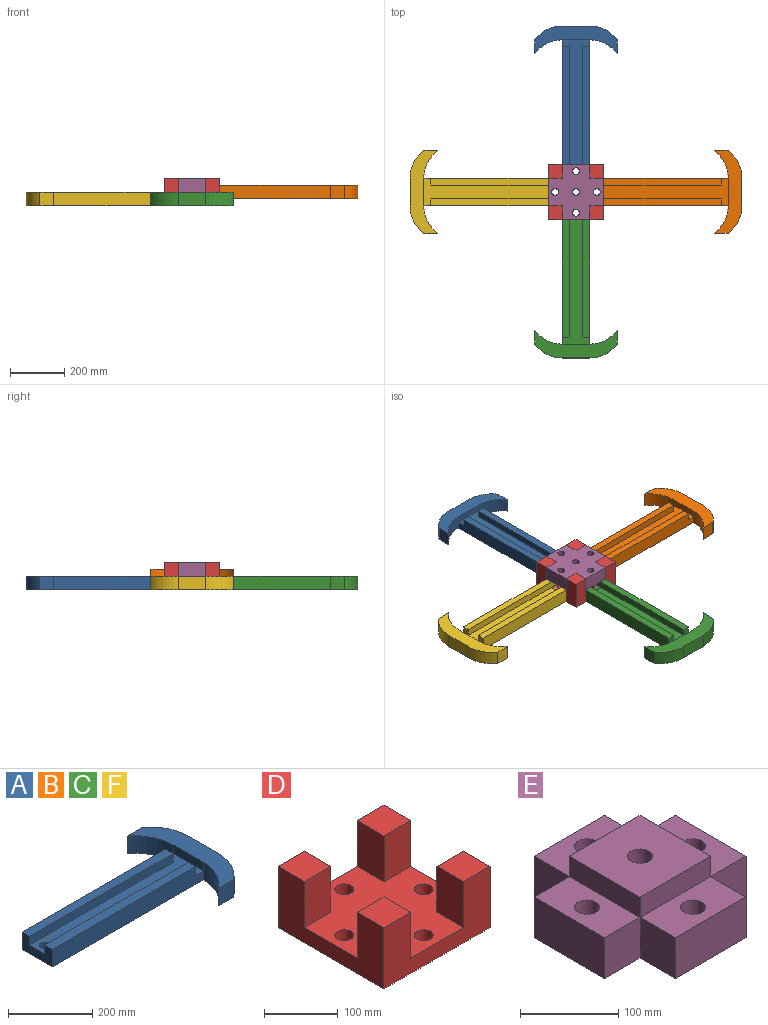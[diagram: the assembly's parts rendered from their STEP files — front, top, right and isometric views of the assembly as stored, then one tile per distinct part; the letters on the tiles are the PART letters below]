
ASSEMBLY  parts=6 mates=5
PART A: 21 faces, bbox 558.8x304.8x50.8 mm
  f0: plane 508x50.8mm, normal (0,-1,0), area 25161.2mm2, adj f4,f5,f12,f14,f19,f20
  f1: plane 508x50.8mm, normal (0,1,0), area 25161.2mm2, adj f11,f12,f13,f14,f16,f20
  f2: cylinder r=12.7mm len=25.4mm, axis (0,0,-1), area 2026.8mm2, adj f14,f20
  f3: plane 304.8x101.6mm, normal (0,0,1), area 15483.8mm2, adj f5,f6,f7,f8,f9,f10,f11,f15
  f4: plane 482.6x25.4mm, normal (0,0,1), area 12258mm2, adj f0,f12,f18,f19
  f5: cylinder r=127mm len=101.6mm, axis (0,0,-1), area 5982.5mm2, adj f0,f3,f6,f14,f15
  f6: plane 50.8x50.8mm, normal (0,-1,0), area 2580.6mm2, adj f3,f5,f7,f14
  f7: cylinder r=127mm len=101.6mm, axis (0,0,-1), area 5982.5mm2, adj f3,f6,f8,f14
  f8: plane 101.6x50.8mm, normal (1,0,0), area 5161.3mm2, adj f3,f7,f9,f14
  f9: cylinder r=127mm len=101.6mm, axis (0,0,-1), area 5982.5mm2, adj f3,f8,f10,f14
  f10: plane 50.8x50.8mm, normal (0,1,0), area 2580.6mm2, adj f3,f9,f11,f14
  f11: cylinder r=127mm len=101.6mm, axis (0,0,-1), area 5982.5mm2, adj f1,f3,f10,f14,f15
  f12: plane 101.6x50.8mm, normal (-1,0,0), area 3871mm2, adj f0,f1,f4,f13,f14,f17,f18,f20
  f13: plane 482.6x25.4mm, normal (0,0,1), area 12258mm2, adj f1,f12,f16,f17
  f14: plane 558.8x304.8mm, normal (0,0,-1), area 66589.9mm2, adj f0,f1,f2,f5,f6,f7,f8,f9
  f15: plane 101.6x25.4mm, normal (-1,0,0), area 2580.6mm2, adj f3,f5,f11,f20
  f16: plane 25.4x25.4mm, normal (1,0,0), area 645.2mm2, adj f1,f13,f17,f20
  f17: plane 482.6x25.4mm, normal (0,-1,0), area 12258mm2, adj f12,f13,f16,f20
  f18: plane 482.6x25.4mm, normal (0,1,0), area 12258mm2, adj f4,f12,f19,f20
  f19: plane 25.4x25.4mm, normal (1,0,0), area 645.2mm2, adj f0,f4,f18,f20
  f20: plane 508x101.6mm, normal (0,0,1), area 26590mm2, adj f0,f1,f2,f12,f15,f16,f17,f18
PART B: same geometry as A
PART C: same geometry as A
PART D: 23 faces, bbox 203.2x203.2x101.6 mm
  f0: plane 203.2x101.6mm, normal (1,0,0), area 12903.2mm2, adj f5,f8,f9,f10,f13,f20,f21,f22
  f1: cylinder r=12.7mm len=25.4mm, axis (0,0,-1), area 2026.8mm2, adj f13,f22
  f2: cylinder r=12.7mm len=25.4mm, axis (0,0,-1), area 2026.8mm2, adj f13,f22
  f3: cylinder r=12.7mm len=25.4mm, axis (0,0,-1), area 2026.8mm2, adj f13,f22
  f4: cylinder r=12.7mm len=25.4mm, axis (0,0,-1), area 2026.8mm2, adj f13,f22
  f5: plane 203.2x101.6mm, normal (0,-1,0), area 12903.2mm2, adj f0,f7,f8,f11,f13,f18,f19,f22
  f6: cylinder r=12.7mm len=25.4mm, axis (0,0,-1), area 2026.8mm2, adj f13,f22
  f7: plane 50.8x50.8mm, normal (0,0,1), area 2580.6mm2, adj f5,f11,f17,f18
  f8: plane 50.8x50.8mm, normal (0,0,1), area 2580.6mm2, adj f0,f5,f19,f20
  f9: plane 50.8x50.8mm, normal (0,0,1), area 2580.6mm2, adj f0,f10,f14,f21
  f10: plane 203.2x101.6mm, normal (0,1,0), area 12903.2mm2, adj f0,f9,f11,f12,f13,f14,f15,f22
  f11: plane 203.2x101.6mm, normal (-1,0,0), area 12903.2mm2, adj f5,f7,f10,f12,f13,f16,f17,f22
  f12: plane 50.8x50.8mm, normal (0,0,1), area 2580.6mm2, adj f10,f11,f15,f16
  f13: plane 203.2x203.2mm, normal (0,0,-1), area 38756.7mm2, adj f0,f1,f2,f3,f4,f5,f6,f10
  f14: plane 76.2x50.8mm, normal (-1,0,0), area 3871mm2, adj f9,f10,f21,f22
  f15: plane 76.2x50.8mm, normal (1,0,0), area 3871mm2, adj f10,f12,f16,f22
  f16: plane 76.2x50.8mm, normal (0,-1,0), area 3871mm2, adj f11,f12,f15,f22
  f17: plane 76.2x50.8mm, normal (0,1,0), area 3871mm2, adj f7,f11,f18,f22
  f18: plane 76.2x50.8mm, normal (1,0,0), area 3871mm2, adj f5,f7,f17,f22
  f19: plane 76.2x50.8mm, normal (-1,0,0), area 3871mm2, adj f5,f8,f20,f22
  f20: plane 76.2x50.8mm, normal (0,1,0), area 3871mm2, adj f0,f8,f19,f22
  f21: plane 76.2x50.8mm, normal (0,-1,0), area 3871mm2, adj f0,f9,f14,f22
  f22: plane 203.2x203.2mm, normal (0,0,1), area 28434.1mm2, adj f0,f1,f2,f3,f4,f5,f6,f10
PART E: 27 faces, bbox 203.2x203.2x76.2 mm
  f0: plane 50.8x50.8mm, normal (0,1,0), area 2580.6mm2, adj f10,f12,f13,f22
  f1: plane 101.6x25.4mm, normal (0,1,0), area 2580.6mm2, adj f4,f6,f9,f26
  f2: plane 50.8x50.8mm, normal (0,-1,0), area 2580.6mm2, adj f10,f14,f16,f18
  f3: plane 50.8x50.8mm, normal (0,-1,0), area 2580.6mm2, adj f10,f12,f13,f17
  f4: plane 101.6x25.4mm, normal (1,0,0), area 2580.6mm2, adj f1,f8,f9,f13
  f5: plane 50.8x50.8mm, normal (0,1,0), area 2580.6mm2, adj f10,f14,f16,f25
  f6: plane 101.6x25.4mm, normal (-1,0,0), area 2580.6mm2, adj f1,f8,f9,f16
  f7: cylinder r=12.7mm len=76.2mm, axis (0,0,-1), area 6080.5mm2, adj f9,f10
  f8: plane 101.6x25.4mm, normal (0,-1,0), area 2580.6mm2, adj f4,f6,f9,f21
  f9: plane 101.6x101.6mm, normal (0,0,1), area 9815.9mm2, adj f1,f4,f6,f7,f8
  f10: plane 203.2x203.2mm, normal (0,0,-1), area 28434.1mm2, adj f0,f2,f3,f5,f7,f11,f12,f14
  f11: cylinder r=12.7mm len=50.8mm, axis (0,0,-1), area 4053.7mm2, adj f10,f13
  f12: plane 101.6x50.8mm, normal (1,0,0), area 5161.3mm2, adj f0,f3,f10,f13
  f13: plane 101.6x50.8mm, normal (0,0,1), area 4654.6mm2, adj f0,f3,f4,f11,f12
  f14: plane 101.6x50.8mm, normal (-1,0,0), area 5161.3mm2, adj f2,f5,f10,f16
  f15: cylinder r=12.7mm len=50.8mm, axis (0,0,-1), area 4053.7mm2, adj f10,f16
  f16: plane 101.6x50.8mm, normal (0,0,1), area 4654.6mm2, adj f2,f5,f6,f14,f15
  f17: plane 50.8x50.8mm, normal (1,0,0), area 2580.6mm2, adj f3,f10,f20,f21
  f18: plane 50.8x50.8mm, normal (-1,0,0), area 2580.6mm2, adj f2,f10,f20,f21
  f19: cylinder r=12.7mm len=50.8mm, axis (0,0,-1), area 4053.7mm2, adj f10,f21
  f20: plane 101.6x50.8mm, normal (0,-1,0), area 5161.3mm2, adj f10,f17,f18,f21
  f21: plane 101.6x50.8mm, normal (0,0,1), area 4654.6mm2, adj f8,f17,f18,f19,f20
  f22: plane 50.8x50.8mm, normal (1,0,0), area 2580.6mm2, adj f0,f10,f23,f26
  f23: plane 101.6x50.8mm, normal (0,1,0), area 5161.3mm2, adj f10,f22,f25,f26
  f24: cylinder r=12.7mm len=50.8mm, axis (0,0,-1), area 4053.7mm2, adj f10,f26
  f25: plane 50.8x50.8mm, normal (-1,0,0), area 2580.6mm2, adj f5,f10,f23,f26
  f26: plane 101.6x50.8mm, normal (0,0,1), area 4654.6mm2, adj f1,f22,f23,f24,f25
PART F: same geometry as A
PLACE A rot(axis=(0,0,1),90deg) t=(20.98,314.66,-54.18)mm
PLACE B t=(325.78,9.86,-28.78)mm
PLACE C rot(axis=(0,0,-1),90deg) t=(20.98,-294.94,-54.18)mm
PLACE D t=(20.98,9.86,-3.38)mm fixed
PLACE E rot(axis=(1,0,0),180deg) t=(20.98,9.86,47.42)mm
PLACE F rot(axis=(0,0,1),180deg) t=(-283.82,9.86,-54.18)mm
MATE fastened B.f2 <-> D.f1  axis (0,0,-1) through (97.18,9.86,-28.78)mm
MATE fastened E.f7 <-> D.f4  axis (0,0,-1) through (20.98,9.86,-28.78)mm
MATE fastened C.f2 <-> D.f6  axis (0,0,-1) through (20.98,-66.34,-54.18)mm
MATE fastened A.f2 <-> D.f2  axis (0,0,-1) through (20.98,86.06,-54.18)mm
MATE fastened F.f2 <-> D.f3  axis (0,0,1) through (-55.22,9.86,-28.78)mm
